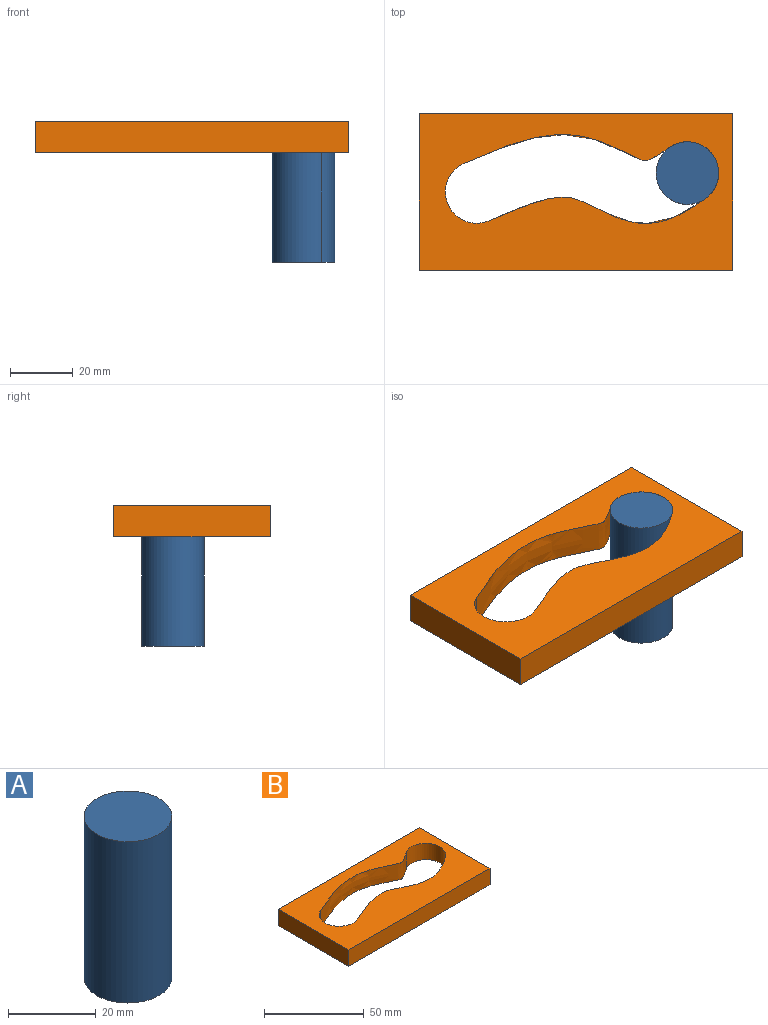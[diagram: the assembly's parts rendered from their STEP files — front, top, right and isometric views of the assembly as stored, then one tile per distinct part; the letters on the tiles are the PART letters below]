
ASSEMBLY  parts=2 mates=1
PART A: 4 faces, bbox 20x20x45 mm
  f0: cylinder r=10mm len=45mm, axis (0,0,1), area 2826.1mm2, adj f1,f2,f3
  f1: extruded ~45x0.02mm, area 1.3mm2, adj f0,f2,f3
  f2: plane 20x20mm, normal (0,0,-1), area 314.2mm2, adj f0,f1
  f3: plane 20x20mm, normal (0,0,1), area 314.2mm2, adj f0,f1
PART B: 10 faces, bbox 100x50x10 mm
  f0: plane 100x10mm, normal (0,-1,0), area 1000mm2, adj f1,f3,f4,f5
  f1: plane 50x10mm, normal (1,0,0), area 500mm2, adj f0,f2,f4,f5
  f2: plane 100x10mm, normal (0,1,0), area 1000mm2, adj f1,f3,f4,f5
  f3: plane 50x10mm, normal (-1,0,0), area 500mm2, adj f0,f2,f4,f5
  f4: plane 100x50mm, normal (0,0,1), area 3248mm2, adj f0,f1,f2,f3,f6,f7,f8,f9
  f5: plane 100x50mm, normal (0,0,-1), area 3248mm2, adj f0,f1,f2,f3,f6,f7,f8,f9
  f6: extruded ~65.59x10mm, area 699.2mm2, adj f4,f5,f7,f9
  f7: cylinder r=10mm len=19.16mm, axis (0,0,1), area 314.2mm2, adj f4,f5,f6,f8
  f8: extruded ~69.02x10mm, area 738.6mm2, adj f4,f5,f7,f9
  f9: cylinder r=10mm len=18.19mm, axis (0,0,1), area 314.2mm2, adj f4,f5,f6,f8
PLACE A rot(axis=(0,0,-1),180deg) t=(71.18,12.11,10)mm
PLACE B at identity fixed
MATE planar A.f0 <-> B.f4  axis (0,0,1) through (35.59,6.05,10)mm
